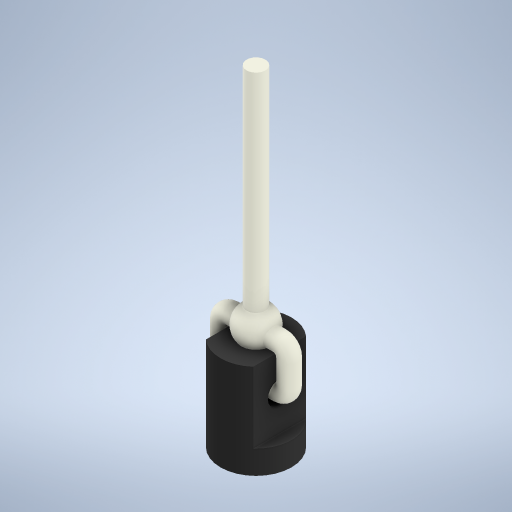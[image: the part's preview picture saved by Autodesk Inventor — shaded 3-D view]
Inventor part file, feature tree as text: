
AUTODESK INVENTOR PART (.ipt)
format: ipt  version: 2024.3 (Build 283343000, 343)  size: 349,184 bytes
history: native  units: mm
features: sketch x7, extrude x4, other x1, sweep x1, plane x1, revolve x1, projected_geometry x1
ambient origin geometry x8: Origin, YZ Plane, XZ Plane, XY Plane, X Axis, Y Axis, Z Axis, Center Point
bodies: Body1 (feature_tree)
feature tree (16):
  other  "솔리드1"
  extrude  "돌출1"  Depth=1.0mm TaperAngle=0.0deg
  extrude  "돌출5"  Depth=2.0mm
  extrude  "돌출6"  Depth=1.0mm
  extrude  "Extrusion7"  Depth=0.4mm TaperAngle=0.0deg
  sweep  "Sweep1"
  plane  "Work Plane2"
  revolve  "Revolution2"  [1 undecoded]
  sketch  "스케치2"
  sketch  "스케치4"
  sketch  "스케치6"
  sketch  "Sketch7"  dims[d0=3.0mm d1=1.0mm d2=0.0mm]
  sketch  "Sketch8"  dims[d6=1.8mm d7=2.0mm]
  sketch  "Sketch9"  dims[d20=3.0mm d21=0.0mm d22=1.0mm]
  projected_geometry  "Projected Loop2"
  sketch  "Sketch11"  dims[d23=1.5mm d24=3.0mm d25=0.0mm d26=0.8mm d27=10.0mm d28=0.0mm d29=0.4mm d30=1.4mm d32=0.4mm d33=0.4mm d34=0.78mm d35=0.0mm d36=0.0mm d39=0.5mm d40=1.6mm d41=90.0deg]
note: 1 required parameter value undecoded (feature->parameter linkage not recoverable at this tier; creation-order binding heuristic only, values carry confidence <= 0.55)
